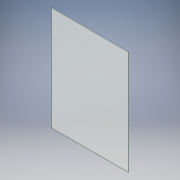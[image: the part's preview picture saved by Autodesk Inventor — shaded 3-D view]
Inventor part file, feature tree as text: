
AUTODESK INVENTOR PART (.ipt)
format: ipt  version: 2017 (Build 210142000, 142)  size: 91,136 bytes
history: native  units: in
note: dims shown in document units (in); Inventor stores cm internally (conversion verified against a paired STEP export)
features: extrude x1, sketch x1
ambient origin geometry x8: Origin, YZ Plane, XZ Plane, XY Plane, X Axis, Y Axis, Z Axis, Center Point
bodies: Solid1 (feature_tree)
feature tree (2):
  extrude  "Extrusion1"  Depth=23.0in
  sketch  "Sketch1"  dims[d0=17.0in d1=23.0in d2=0.125in d3=0.0in]
